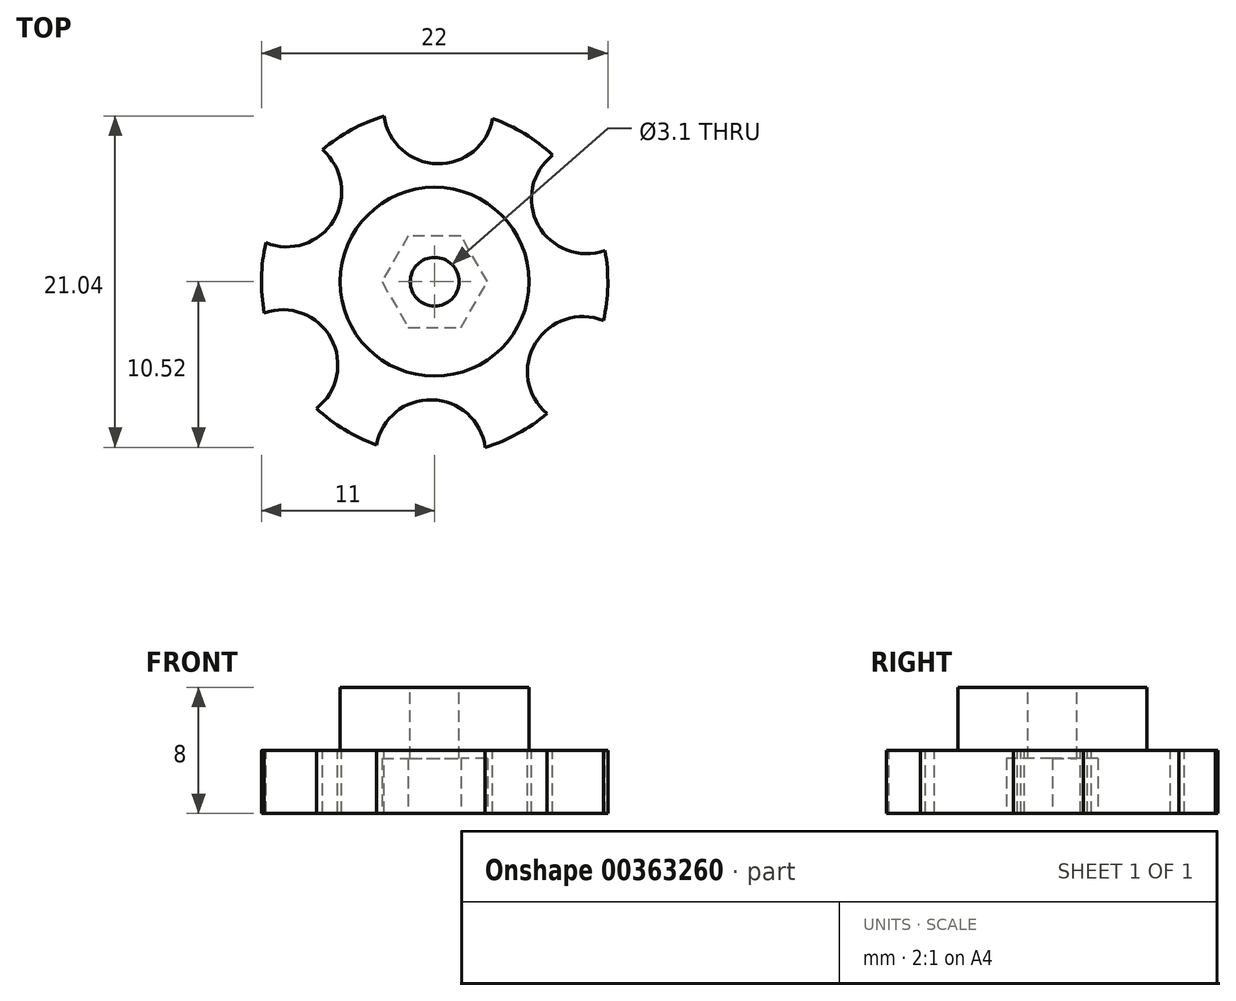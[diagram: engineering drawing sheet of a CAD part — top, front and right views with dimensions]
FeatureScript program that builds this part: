
annotation { "Feature Type Name" : "Feature", "Feature Type Description" : "" }
export const myFeature = defineFeature(function(context is Context, id is Id, definition is map)
    precondition{}
    {
        {
            var Q0;
            Q0=qCreatedBy(makeId("Top.planeOp"),FACE);
            var sketch = newSketch(context, id + "F0", { "sketchPlane" : qUnion([Q0])});
            skCircle(sketch, "E0", {"center": v(0, 0) * mm, "radius": 11 * mm});
            skSolve(sketch);
        }
        {
            var Q0;
            Q0=makeQuery(id+"F0.imprint","IMPRINT",FACE,{"disambiguationData":[TD([[makeQuery(id+"F0.imprint","IMPRINT",EDGE,{"derivedFrom":sQuery(id+"F0.wireOp",EDGE,"E0")}),1.0]])]});
            extrude(context, id + "F1", {"entities" : qUnion([Q0]), "depth" : 4 * mm});
        }
        {
            var Q0;
            Q0=makeQuery(id+"F1.opExtrude","CAP_FACE",FACE,{"disambiguationData":[OSD([sQuery(id+"F0.wireOp",EDGE,"E0")])],"isStart":false});
            var sketch = newSketch(context, id + "F2", { "sketchPlane" : qUnion([Q0])});
            skCircle(sketch, "E1", {"center": v(0.25, 11) * mm, "radius": 3.5 * mm});
            skSolve(sketch);
        }
        {
            var Q0;
            Q0=qSketchRegion(id+"F2",true);
            var Q1;
            Q1=makeQuery(id+"F1.opExtrude","CAP_FACE",FACE,{"disambiguationData":[OSD([sQuery(id+"F0.wireOp",EDGE,"E0")])],"isStart":true});
            extrude(context, id + "F3", {"entities" : qUnion([Q0]), "endBound" : BoundingType.UP_TO_SURFACE, "oppositeDirection" : true, "endBoundEntityFace" : qUnion([Q1]), "depth" : 4 * mm});
        }
        {
            var Q0;
            Q0=makeQuery(id+"F3.opExtrude","SWEPT_BODY",BODY,{"disambiguationData":[OSD([sQuery(id+"F2.wireOp",EDGE,"E1")])]});
            var Q1;
            Q1=makeQuery(id+"F1.opExtrude","CAP_EDGE",EDGE,{"disambiguationData":[OSD([sQuery(id+"F0.wireOp",EDGE,"E0")])],"isStart":false});
            circularPattern(context, id + "F4", {"operationType" : NewBodyOperationType.REMOVE, "entities" : qUnion([Q0]), "axis" : qUnion([Q1]), "angle" : 360 * degree, "instanceCount" : 6, "equalSpace" : true});
        }
        {
            var Q0;
            Q0=makeQuery(id+"F1.opExtrude","CAP_FACE",FACE,{"disambiguationData":[OSD([sQuery(id+"F0.wireOp",EDGE,"E0")])],"isStart":false});
            var sketch = newSketch(context, id + "F5", { "sketchPlane" : qUnion([Q0])});
            skCircle(sketch, "E2", {"center": v(0, 0) * mm, "radius": 6 * mm});
            skSolve(sketch);
        }
        {
            var Q0;
            Q0=makeQuery(id+"F5.imprint","IMPRINT",FACE,{"disambiguationData":[TD([[makeQuery(id+"F5.imprint","IMPRINT",EDGE,{"derivedFrom":sQuery(id+"F5.wireOp",EDGE,"E2")}),1.0]])]});
            extrude(context, id + "F6", {"entities" : qUnion([Q0]), "operationType" : NewBodyOperationType.ADD, "depth" : 4 * mm});
        }
        {
            var Q0;
            Q0=makeQuery(id+"F1.opExtrude","CAP_FACE",FACE,{"disambiguationData":[OSD([sQuery(id+"F0.wireOp",EDGE,"E0")])],"isStart":true});
            var sketch = newSketch(context, id + "F7", { "sketchPlane" : qUnion([Q0])});
            skCircle(sketch, "E3.cCircle", {"center": v(0, 0) * mm, "radius": 2.9 * mm, "construction": true});
            skLineSegment(sketch, "E3.0", {"start": v(-1.67, 2.9) * mm, "end": v(1.67, 2.9) * mm});
            skLineSegment(sketch, "E3.1", {"start": v(1.67, 2.9) * mm, "end": v(3.35, 0) * mm});
            skLineSegment(sketch, "E3.2", {"start": v(3.35, 0) * mm, "end": v(1.67, -2.9) * mm});
            skLineSegment(sketch, "E3.3", {"start": v(1.67, -2.9) * mm, "end": v(-1.67, -2.9) * mm});
            skLineSegment(sketch, "E3.4", {"start": v(-1.67, -2.9) * mm, "end": v(-3.35, 0) * mm});
            skLineSegment(sketch, "E3.5", {"start": v(-3.35, 0) * mm, "end": v(-1.67, 2.9) * mm});
            skPoint(sketch, "E3.0.midPoint", {"position": v(0, 2.9) * mm});
            skSolve(sketch);
        }
        {
            var Q0;
            Q0=makeQuery(id+"F7.imprint","IMPRINT",FACE,{"disambiguationData":[TD([[makeQuery(id+"F7.imprint","IMPRINT",EDGE,{"derivedFrom":sQuery(id+"F7.wireOp",EDGE,"E3.0")}),-1.0]])]});
            extrude(context, id + "F8", {"entities" : qUnion([Q0]), "operationType" : NewBodyOperationType.REMOVE, "oppositeDirection" : true, "depth" : 3.5 * mm});
        }
        {
            var Q0;
            Q0=makeQuery(id+"F6.opExtrude","CAP_FACE",FACE,{"disambiguationData":[OSD([sQuery(id+"F5.wireOp",EDGE,"E2")])],"isStart":false});
            var sketch = newSketch(context, id + "F9", { "sketchPlane" : qUnion([Q0])});
            skCircle(sketch, "E4", {"center": v(0, 0) * mm, "radius": 1.55 * mm});
            skSolve(sketch);
        }
        {
            var Q0;
            Q0=makeQuery(id+"F9.imprint","IMPRINT",FACE,{"disambiguationData":[TD([[makeQuery(id+"F9.imprint","IMPRINT",EDGE,{"derivedFrom":sQuery(id+"F9.wireOp",EDGE,"E4")}),1.0]])]});
            extrude(context, id + "F10", {"entities" : qUnion([Q0]), "operationType" : NewBodyOperationType.REMOVE, "endBound" : BoundingType.THROUGH_ALL, "oppositeDirection" : true, "depth" : 25 * mm});
        }
    });
